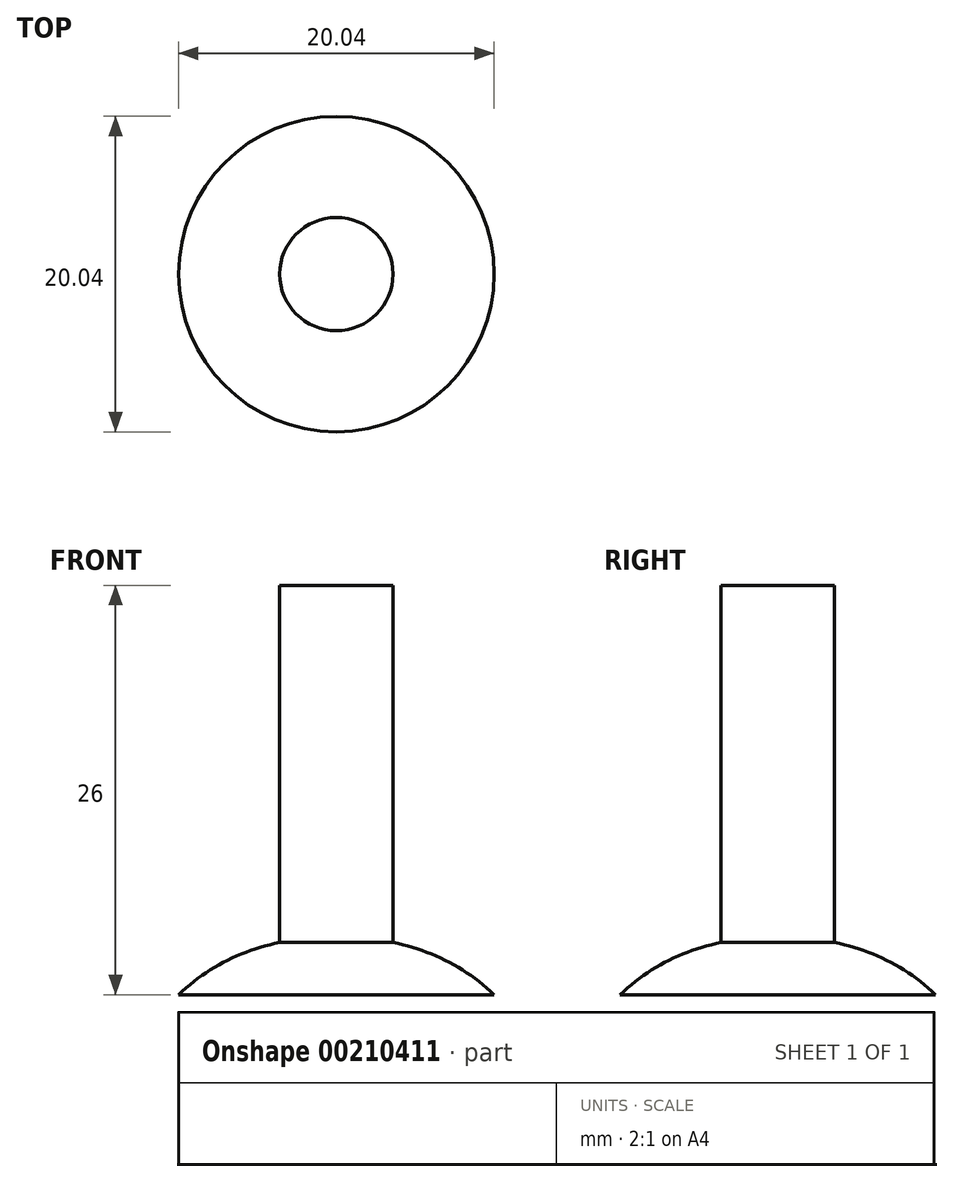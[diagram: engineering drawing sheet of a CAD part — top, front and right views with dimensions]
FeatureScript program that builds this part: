
annotation { "Feature Type Name" : "Feature", "Feature Type Description" : "" }
export const myFeature = defineFeature(function(context is Context, id is Id, definition is map)
    precondition{}
    {
        {
            var Q0;
            Q0=qCreatedBy(makeId("Front.planeOp"),FACE);
            var sketch = newSketch(context, id + "F0", { "sketchPlane" : qUnion([Q0])});
            skLineSegment(sketch, "E0", {"start": v(0, 0) * mm, "end": v(0, 3.5) * mm});
            skLineSegment(sketch, "E1", {"start": v(0, 0) * mm, "end": v(0, 9.33) * mm, "construction": true});
            skArc(sketch, "E2", {"start": v(10.02, 0) * mm, "mid": v(5.39, 2.83) * mm, "end": v(0, 3.5) * mm});
            skLineSegment(sketch, "E3", {"start": v(0, 0) * mm, "end": v(10.02, 0) * mm});
            skSolve(sketch);
        }
        {
            var Q0;
            Q0=makeQuery(id+"F0.imprint","IMPRINT",FACE,{"disambiguationData":[TD([[makeQuery(id+"F0.imprint","IMPRINT",EDGE,{"derivedFrom":sQuery(id+"F0.wireOp",EDGE,"E0")}),-1.0]])]});
            var Q1;
            Q1=sQuery(id+"F0.wireOp",EDGE,"E1");
            revolve(context, id + "F1", {"entities" : qUnion([Q0]), "axis" : qUnion([Q1]), "revolveType" : RevolveType.FULL});
        }
        {
            var Q0;
            Q0=qCreatedBy(makeId("Top.planeOp"),FACE);
            var sketch = newSketch(context, id + "F2", { "sketchPlane" : qUnion([Q0])});
            skCircle(sketch, "E4", {"center": v(0, 0) * mm, "radius": 3.6 * mm});
            skSolve(sketch);
        }
        {
            var Q0;
            Q0 = qSketchRegion(id + "F2", true);
            extrude(context, id + "F3", {"entities" : qUnion([Q0]), "operationType" : NewBodyOperationType.ADD, "depth" : 26 * mm});
        }
    });
